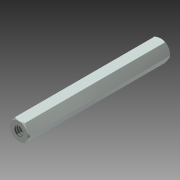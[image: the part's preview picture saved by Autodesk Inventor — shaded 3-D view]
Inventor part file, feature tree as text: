
AUTODESK INVENTOR PART (.ipt)
format: ipt  version: 2013 (Build 170138000, 138)  size: 121,856 bytes
history: native  units: mm (DEFAULTED — no unit token found)
features: sketch x4, hole x2, extrude x1, plane x1, revolve x1
ambient origin geometry x8: Origin, YZ Plane, XZ Plane, XY Plane, X Axis, Y Axis, Z Axis, Center Point
bodies: Solid1 (feature_tree)
feature tree (9):
  extrude  "Extrusion1"  Depth=50.8mm TaperAngle=0.0deg
  plane  "Work Plane1"
  revolve  "Revolution1"  [1 undecoded]
  hole  "Hole2"  [1 undecoded]
  hole  "Hole3"  [1 undecoded]
  sketch  "Sketch1"  dims[d0=6.35mm d1=50.8mm d2=0.0mm]
  sketch  "Sketch3"  dims[d4=-3.175mm d5=0.508mm]
  sketch  "Sketch5"  dims[d6=0.508mm d7=0.508mm]
  sketch  "Sketch6"  dims[d8=0.508mm d9=0.508mm d10=0.508mm d11=0.508mm d12=0.508mm d13=7.3152mm d14=0.0mm d15=50.8mm d16=0.0mm d17=90.0deg d25=3.302mm d26=12.7mm d27=9.525mm d28=6.35mm d29=14.3117mm d30=12.7mm d31=20.594885mm d32=3.302mm d33=12.7mm d34=9.525mm d35=6.35mm d36=14.3117mm d37=12.7mm d38=20.594885mm]
note: 3 required parameter values undecoded (feature->parameter linkage not recoverable at this tier; creation-order binding heuristic only, values carry confidence <= 0.55)